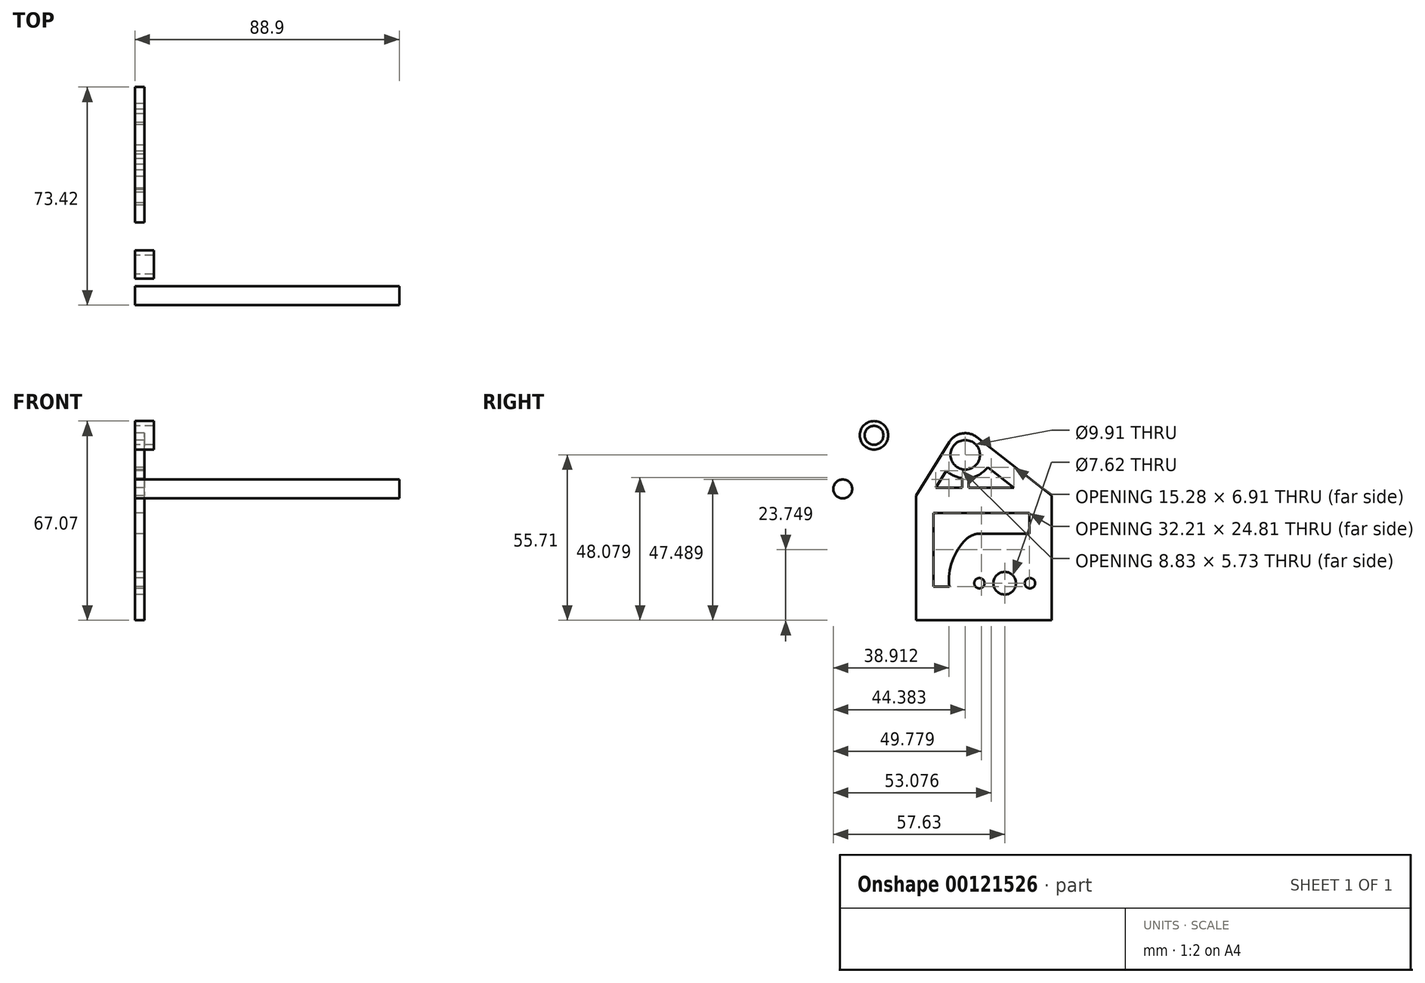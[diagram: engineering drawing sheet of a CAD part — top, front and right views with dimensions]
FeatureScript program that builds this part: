
annotation { "Feature Type Name" : "Feature", "Feature Type Description" : "" }
export const myFeature = defineFeature(function(context is Context, id is Id, definition is map)
    precondition{}
    {
        {
            var Q0;
            Q0=qCreatedBy(makeId("Right.planeOp"),FACE);
            var sketch = newSketch(context, id + "F0", { "sketchPlane" : qUnion([Q0])});
            skLineSegment(sketch, "E0.bottom", {"start": v(-29.8, -28.35) * mm, "end": v(15.8, -28.35) * mm});
            skLineSegment(sketch, "E0.left", {"start": v(-29.8, -28.35) * mm, "end": v(-29.8, 13.56) * mm});
            skLineSegment(sketch, "E0.right", {"start": v(15.8, -28.35) * mm, "end": v(15.8, 13.56) * mm});
            skLineSegment(sketch, "E1", {"start": v(-29.8, 13.56) * mm, "end": v(-18.65, 31.62) * mm});
            skLineSegment(sketch, "E2", {"start": v(-9.33, 33.28) * mm, "end": v(15.8, 13.56) * mm});
            skPoint(sketch, "E3.visualSharp", {"position": v(-14.92, 37.67) * mm});
            skArc(sketch, "E3.filletArc", {"start": v(-9.33, 33.28) * mm, "mid": v(-14.36, 34.54) * mm, "end": v(-18.65, 31.62) * mm});
            skLineSegment(sketch, "E4", {"start": v(0, -28.35) * mm, "end": v(0, -15.85) * mm});
            skCircle(sketch, "E5", {"center": v(0, -15.85) * mm, "radius": 3.81 * mm});
            skLineSegment(sketch, "E6", {"start": v(0, -15.85) * mm, "end": v(8.5, -15.85) * mm});
            skCircle(sketch, "E7", {"center": v(8.5, -15.85) * mm, "radius": 1.75 * mm});
            skLineSegment(sketch, "E8.MirrorCS", {"start": v(0, -15.85) * mm, "end": v(-8.5, -15.85) * mm});
            skCircle(sketch, "E9.MirrorC", {"center": v(-8.5, -15.85) * mm, "radius": 1.75 * mm});
            skCircle(sketch, "E10", {"center": v(-13.25, 27.36) * mm, "radius": 4.95 * mm});
            skArc(sketch, "E11", {"start": v(-19.6, 22) * mm, "mid": v(-12.4, 19.47) * mm, "end": v(-5.72, 23.19) * mm});
            skLineSegment(sketch, "E12", {"start": v(-19.6, 22) * mm, "end": v(-23.14, 16.27) * mm});
            skLineSegment(sketch, "E13", {"start": v(-23.14, 16.27) * mm, "end": v(3.09, 16.27) * mm});
            skLineSegment(sketch, "E14", {"start": v(3.09, 16.27) * mm, "end": v(-5.72, 23.19) * mm});
            skLineSegment(sketch, "E15", {"start": v(-14.3, 19.5) * mm, "end": v(-14.3, 16.27) * mm});
            skLineSegment(sketch, "E16", {"start": v(-12.2, 19.5) * mm, "end": v(-12.2, 16.27) * mm});
            skLineSegment(sketch, "E17", {"start": v(-23.95, 7.8) * mm, "end": v(-23.95, -17) * mm});
            skLineSegment(sketch, "E18", {"start": v(-23.95, -17) * mm, "end": v(-18.6, -17) * mm});
            skArc(sketch, "E19", {"start": v(-12.86, -0.98) * mm, "mid": v(-17.6, -8.32) * mm, "end": v(-18.6, -17) * mm});
            skLineSegment(sketch, "E20", {"start": v(-23.95, 7.8) * mm, "end": v(8.25, 7.8) * mm});
            skLineSegment(sketch, "E21", {"start": v(8.25, 7.8) * mm, "end": v(8.25, 0.8) * mm});
            skLineSegment(sketch, "E22", {"start": v(8.25, 0.8) * mm, "end": v(-8.45, 0.8) * mm});
            skPoint(sketch, "E23.visualSharp", {"position": v(-10.72, 0.8) * mm});
            skArc(sketch, "E23.filletArc", {"start": v(-8.45, 0.8) * mm, "mid": v(-10.82, 0.34) * mm, "end": v(-12.86, -0.98) * mm});
            skSolve(sketch);
        }
        {
            var Q0;
            Q0 = qSketchRegion(id + "F0", true);
            var Q1;
            {var subQ0=sQuery(id+"F0.wireOp",EDGE,"E15");Q1=makeQuery(id+"F0.imprint","IMPRINT",FACE,{"disambiguationData":[TD([[makeQuery(id+"F0.imprint","IMPRINT",EDGE,{"derivedFrom":subQ0}),1.0]])]});}
            extrude(context, id + "F1", {"entities" : qUnion([Q0, Q1]), "depth" : 3.17 * mm});
        }
        {
            var Q0;
            Q0=qCreatedBy(makeId("Right.planeOp"),FACE);
            var sketch = newSketch(context, id + "F2", { "sketchPlane" : qUnion([Q0])});
            skCircle(sketch, "E24", {"center": v(-43.95, 33.93) * mm, "radius": 3.18 * mm});
            skCircle(sketch, "E25", {"center": v(-43.95, 33.93) * mm, "radius": 4.79 * mm});
            skSolve(sketch);
        }
        {
            var Q0;
            Q0 = qSketchRegion(id + "F2", true);
            extrude(context, id + "F3", {"entities" : qUnion([Q0]), "depth" : 6.35 * mm});
        }
        {
            var Q0;
            Q0=qCreatedBy(makeId("Right.planeOp"),FACE);
            var sketch = newSketch(context, id + "F4", { "sketchPlane" : qUnion([Q0])});
            skCircle(sketch, "E26", {"center": v(-54.46, 15.87) * mm, "radius": 3.18 * mm});
            skSolve(sketch);
        }
        {
            var Q0;
            Q0 = qSketchRegion(id + "F4", true);
            extrude(context, id + "F5", {"entities" : qUnion([Q0]), "depth" : 88.9 * mm});
        }
    });
